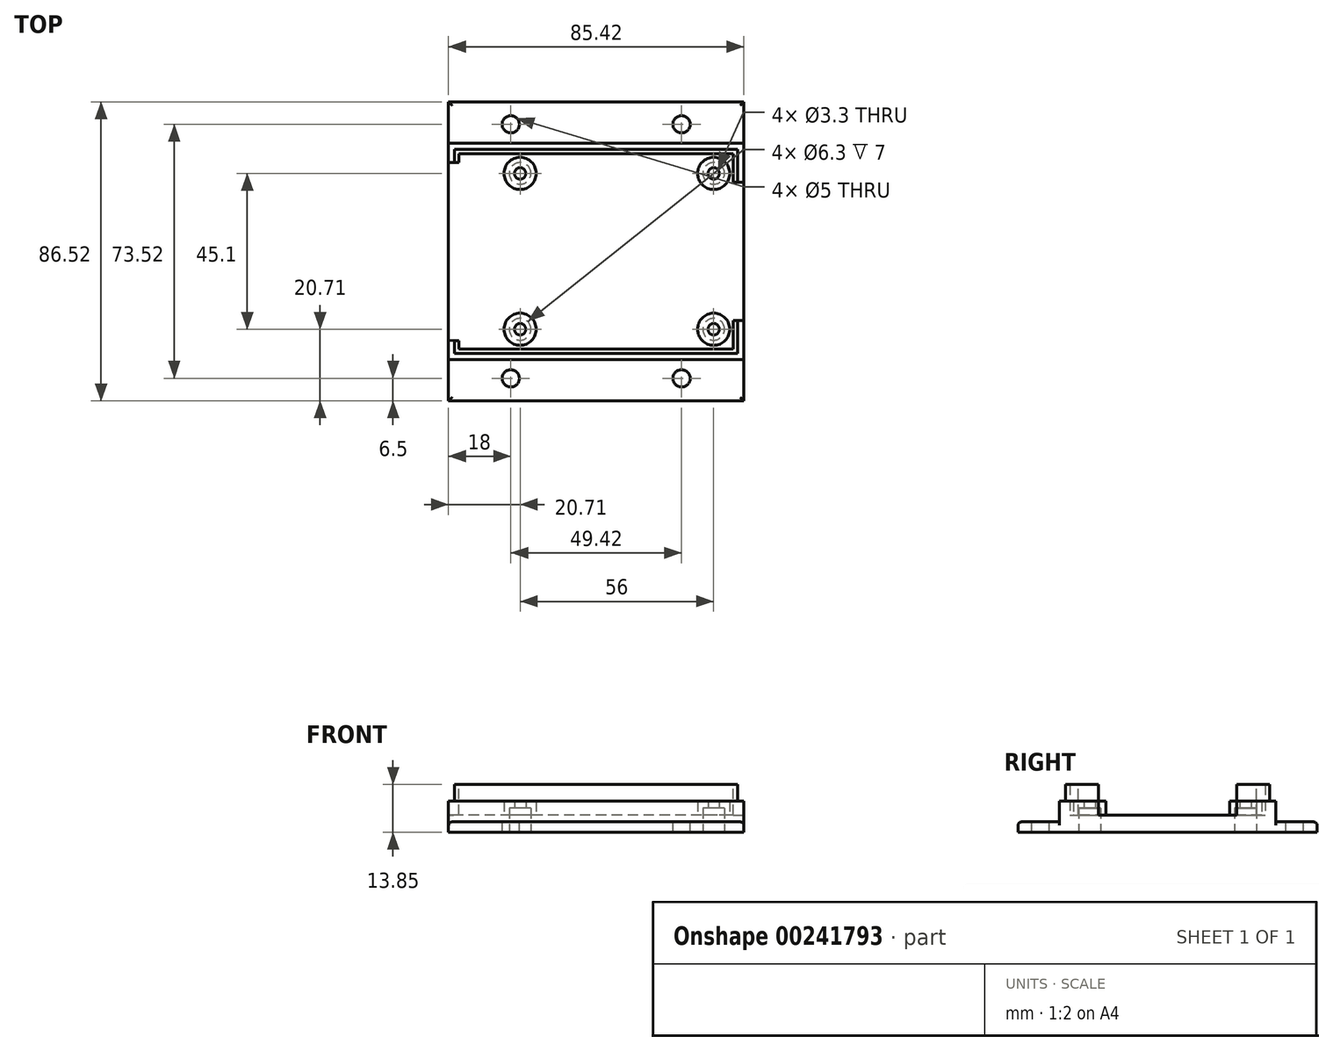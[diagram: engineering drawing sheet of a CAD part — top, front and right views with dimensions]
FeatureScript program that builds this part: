
annotation { "Feature Type Name" : "Feature", "Feature Type Description" : "" }
export const myFeature = defineFeature(function(context is Context, id is Id, definition is map)
    precondition{}
    {
        {
            var Q0;
            Q0=qCreatedBy(makeId("Top.planeOp"),FACE);
            var sketch = newSketch(context, id + "F0", { "sketchPlane" : qUnion([Q0])});
            skLineSegment(sketch, "E0.bottom", {"start": v(37.2, -25.76) * mm, "end": v(-37.2, -25.76) * mm, "construction": true});
            skLineSegment(sketch, "E0.top", {"start": v(37.2, 25.76) * mm, "end": v(-37.2, 25.76) * mm, "construction": true});
            skLineSegment(sketch, "E0.left", {"start": v(37.2, -25.76) * mm, "end": v(37.2, 25.76) * mm, "construction": true});
            skLineSegment(sketch, "E0.right", {"start": v(-37.2, -25.76) * mm, "end": v(-37.2, 25.76) * mm, "construction": true});
            skPoint(sketch, "E0.middle", {"position": v(0, 0) * mm});
            skCircle(sketch, "E1", {"center": v(-22, 22.55) * mm, "radius": 1.65 * mm});
            skCircle(sketch, "E2", {"center": v(34, 22.55) * mm, "radius": 1.65 * mm});
            skCircle(sketch, "E3", {"center": v(-22, -22.55) * mm, "radius": 1.65 * mm});
            skCircle(sketch, "E4", {"center": v(34, -22.55) * mm, "radius": 1.65 * mm});
            skLineSegment(sketch, "E5.0", {"start": v(39.7, 28.26) * mm, "end": v(-39.7, 28.26) * mm});
            skLineSegment(sketch, "E5.1", {"start": v(39.7, -28.26) * mm, "end": v(39.7, 28.26) * mm});
            skLineSegment(sketch, "E5.2", {"start": v(39.7, -28.26) * mm, "end": v(-39.7, -28.26) * mm});
            skLineSegment(sketch, "E5.3", {"start": v(-39.7, -28.26) * mm, "end": v(-39.7, 28.26) * mm});
            skLineSegment(sketch, "E6.0", {"start": v(41.2, 29.76) * mm, "end": v(-41.2, 29.76) * mm});
            skLineSegment(sketch, "E6.1", {"start": v(41.2, -29.76) * mm, "end": v(41.2, 29.76) * mm});
            skLineSegment(sketch, "E6.2", {"start": v(41.2, -29.76) * mm, "end": v(-41.2, -29.76) * mm});
            skLineSegment(sketch, "E6.3", {"start": v(-41.2, -29.76) * mm, "end": v(-41.2, 29.76) * mm});
            skLineSegment(sketch, "E7.0", {"start": v(42.7, 31.26) * mm, "end": v(-42.7, 31.26) * mm});
            skLineSegment(sketch, "E7.1", {"start": v(42.7, -31.26) * mm, "end": v(42.7, 31.26) * mm});
            skLineSegment(sketch, "E7.2", {"start": v(42.7, -31.26) * mm, "end": v(-42.7, -31.26) * mm});
            skLineSegment(sketch, "E7.3", {"start": v(-42.7, -31.26) * mm, "end": v(-42.7, 31.26) * mm});
            skCircle(sketch, "E8.0", {"center": v(-22, 22.55) * mm, "radius": 4.65 * mm});
            skCircle(sketch, "E9.0", {"center": v(34, 22.55) * mm, "radius": 4.65 * mm});
            skCircle(sketch, "E10.0", {"center": v(34, -22.55) * mm, "radius": 4.65 * mm});
            skCircle(sketch, "E11.0", {"center": v(-22, -22.55) * mm, "radius": 4.65 * mm});
            skCircle(sketch, "E12", {"center": v(-22, 22.55) * mm, "radius": 3.15 * mm});
            skCircle(sketch, "E13", {"center": v(34, 22.55) * mm, "radius": 3.15 * mm});
            skCircle(sketch, "E14", {"center": v(34, -22.55) * mm, "radius": 3.15 * mm});
            skCircle(sketch, "E15", {"center": v(-22, -22.55) * mm, "radius": 3.15 * mm});
            skSolve(sketch);
        }
        {
            var Q0;
            Q0=makeQuery(id+"F0.imprint","IMPRINT",FACE,{"disambiguationData":[TD([[makeQuery(id+"F0.imprint","IMPRINT",EDGE,{"derivedFrom":sQuery(id+"F0.wireOp",EDGE,"E5.0")}),1.0]])]});
            extrude(context, id + "F1", {"entities" : qUnion([Q0]), "depth" : 5 * mm, "offsetDistance" : 25 * mm});
        }
        {
            var Q0;
            Q0=makeQuery(id+"F0.imprint","IMPRINT",FACE,{"disambiguationData":[TD([[makeQuery(id+"F0.imprint","IMPRINT",EDGE,{"derivedFrom":sQuery(id+"F0.wireOp",EDGE,"E5.0")}),-1.0]])]});
            extrude(context, id + "F2", {"entities" : qUnion([Q0]), "operationType" : NewBodyOperationType.ADD, "depth" : 13.85 * mm, "offsetDistance" : 25 * mm});
        }
        {
            var Q0;
            Q0=makeQuery(id+"F0.imprint","IMPRINT",FACE,{"disambiguationData":[TD([[makeQuery(id+"F0.imprint","IMPRINT",EDGE,{"derivedFrom":sQuery(id+"F0.wireOp",EDGE,"E6.0")}),-1.0]])]});
            extrude(context, id + "F3", {"entities" : qUnion([Q0]), "operationType" : NewBodyOperationType.ADD, "depth" : 9 * mm, "offsetDistance" : 25 * mm});
        }
        {
            var Q0;
            Q0=makeQuery(id+"F2.opExtrude","CAP_FACE",FACE,{"disambiguationData":[OSD([sQuery(id+"F0.wireOp",EDGE,"E5.0"),sQuery(id+"F0.wireOp",EDGE,"E5.1"),sQuery(id+"F0.wireOp",EDGE,"E5.2"),sQuery(id+"F0.wireOp",EDGE,"E5.3"),sQuery(id+"F0.wireOp",EDGE,"E6.0"),sQuery(id+"F0.wireOp",EDGE,"E6.1"),sQuery(id+"F0.wireOp",EDGE,"E6.2"),sQuery(id+"F0.wireOp",EDGE,"E6.3")])],"isStart":false});
            var sketch = newSketch(context, id + "F4", { "sketchPlane" : qUnion([Q0])});
            skLineSegment(sketch, "E16", {"start": v(-39.7, 25.75) * mm, "end": v(-41.2, 25.75) * mm});
            skLineSegment(sketch, "E17", {"start": v(-39.7, -25.8) * mm, "end": v(-41.2, -25.8) * mm});
            skLineSegment(sketch, "E18", {"start": v(-41.2, 25.75) * mm, "end": v(-42.84, 25.75) * mm});
            skLineSegment(sketch, "E19", {"start": v(-42.84, 25.75) * mm, "end": v(-42.84, -25.8) * mm});
            skLineSegment(sketch, "E20", {"start": v(-42.84, -25.8) * mm, "end": v(-41.2, -25.8) * mm});
            skLineSegment(sketch, "E21", {"start": v(-39.7, -25.8) * mm, "end": v(-39.7, 25.75) * mm});
            skLineSegment(sketch, "E22", {"start": v(39.7, 19.96) * mm, "end": v(43.26, 19.96) * mm});
            skLineSegment(sketch, "E23", {"start": v(43.26, 19.96) * mm, "end": v(43.26, -19.96) * mm});
            skLineSegment(sketch, "E24", {"start": v(43.26, -19.96) * mm, "end": v(39.7, -19.96) * mm});
            skLineSegment(sketch, "E25", {"start": v(39.7, -19.96) * mm, "end": v(39.7, 19.96) * mm});
            skSolve(sketch);
        }
        {
            var Q0;
            {var subQ0=sQuery(id+"F4.wireOp",EDGE,"E18");Q0=makeQuery(id+"F4.imprint","IMPRINT",FACE,{"disambiguationData":[TD([[makeQuery(id+"F4.imprint","IMPRINT",EDGE,{"derivedFrom":subQ0}),1.0]])]});}
            var Q1;
            {var subQ0=sQuery(id+"F4.wireOp",EDGE,"E16");Q1=makeQuery(id+"F4.imprint","IMPRINT",FACE,{"disambiguationData":[TD([[makeQuery(id+"F4.imprint","IMPRINT",EDGE,{"derivedFrom":subQ0}),1.0]])]});}
            var Q2;
            {var subQ0=sQuery(id+"F4.wireOp",EDGE,"E25");Q2=makeQuery(id+"F4.imprint","IMPRINT",FACE,{"disambiguationData":[TD([[makeQuery(id+"F4.imprint","IMPRINT",EDGE,{"derivedFrom":subQ0}),-1.0]])]});}
            var Q3;
            {var subQ0=sQuery(id+"F4.wireOp",EDGE,"E23");Q3=makeQuery(id+"F4.imprint","IMPRINT",FACE,{"disambiguationData":[TD([[makeQuery(id+"F4.imprint","IMPRINT",EDGE,{"derivedFrom":subQ0}),-1.0]])]});}
            extrude(context, id + "F5", {"entities" : qUnion([Q0, Q1, Q2, Q3]), "operationType" : NewBodyOperationType.REMOVE, "oppositeDirection" : true, "depth" : 8.85 * mm, "offsetDistance" : 25 * mm});
        }
        {
            var Q0;
            Q0=makeQuery(id+"F0.imprint","IMPRINT",FACE,{"disambiguationData":[TD([[makeQuery(id+"F0.imprint","IMPRINT",EDGE,{"derivedFrom":sQuery(id+"F0.wireOp",EDGE,"E8.0")}),1.0]])]});
            var Q1;
            Q1=makeQuery(id+"F0.imprint","IMPRINT",FACE,{"disambiguationData":[TD([[makeQuery(id+"F0.imprint","IMPRINT",EDGE,{"derivedFrom":sQuery(id+"F0.wireOp",EDGE,"E9.0")}),1.0]])]});
            var Q2;
            Q2=makeQuery(id+"F0.imprint","IMPRINT",FACE,{"disambiguationData":[TD([[makeQuery(id+"F0.imprint","IMPRINT",EDGE,{"derivedFrom":sQuery(id+"F0.wireOp",EDGE,"E11.0")}),1.0]])]});
            var Q3;
            Q3=makeQuery(id+"F0.imprint","IMPRINT",FACE,{"disambiguationData":[TD([[makeQuery(id+"F0.imprint","IMPRINT",EDGE,{"derivedFrom":sQuery(id+"F0.wireOp",EDGE,"E10.0")}),1.0]])]});
            var Q4;
            Q4=makeQuery(id+"F0.imprint","IMPRINT",FACE,{"disambiguationData":[TD([[makeQuery(id+"F0.imprint","IMPRINT",EDGE,{"derivedFrom":sQuery(id+"F0.wireOp",EDGE,"E3")}),-1.0]])]});
            var Q5;
            Q5=makeQuery(id+"F0.imprint","IMPRINT",FACE,{"disambiguationData":[TD([[makeQuery(id+"F0.imprint","IMPRINT",EDGE,{"derivedFrom":sQuery(id+"F0.wireOp",EDGE,"E1")}),-1.0]])]});
            var Q6;
            Q6=makeQuery(id+"F0.imprint","IMPRINT",FACE,{"disambiguationData":[TD([[makeQuery(id+"F0.imprint","IMPRINT",EDGE,{"derivedFrom":sQuery(id+"F0.wireOp",EDGE,"E2")}),-1.0]])]});
            var Q7;
            Q7=makeQuery(id+"F0.imprint","IMPRINT",FACE,{"disambiguationData":[TD([[makeQuery(id+"F0.imprint","IMPRINT",EDGE,{"derivedFrom":sQuery(id+"F0.wireOp",EDGE,"E4")}),-1.0]])]});
            extrude(context, id + "F6", {"entities" : qUnion([Q0, Q1, Q2, Q3, Q4, Q5, Q6, Q7]), "operationType" : NewBodyOperationType.ADD, "depth" : 9 * mm, "offsetDistance" : 25 * mm});
        }
        {
            var Q0;
            Q0=makeQuery(id+"F0.imprint","IMPRINT",FACE,{"disambiguationData":[TD([[makeQuery(id+"F0.imprint","IMPRINT",EDGE,{"derivedFrom":sQuery(id+"F0.wireOp",EDGE,"E3")}),-1.0]])]});
            var Q1;
            Q1=makeQuery(id+"F0.imprint","IMPRINT",FACE,{"disambiguationData":[TD([[makeQuery(id+"F0.imprint","IMPRINT",EDGE,{"derivedFrom":sQuery(id+"F0.wireOp",EDGE,"E4")}),-1.0]])]});
            var Q2;
            Q2=makeQuery(id+"F0.imprint","IMPRINT",FACE,{"disambiguationData":[TD([[makeQuery(id+"F0.imprint","IMPRINT",EDGE,{"derivedFrom":sQuery(id+"F0.wireOp",EDGE,"E2")}),-1.0]])]});
            var Q3;
            Q3=makeQuery(id+"F0.imprint","IMPRINT",FACE,{"disambiguationData":[TD([[makeQuery(id+"F0.imprint","IMPRINT",EDGE,{"derivedFrom":sQuery(id+"F0.wireOp",EDGE,"E1")}),-1.0]])]});
            extrude(context, id + "F7", {"entities" : qUnion([Q0, Q1, Q2, Q3]), "operationType" : NewBodyOperationType.REMOVE, "depth" : 7 * mm, "offsetDistance" : 25 * mm});
        }
        {
            var Q0;
            Q0=makeQuery(id+"F3.opExtrude","SWEPT_FACE",FACE,{"disambiguationData":[OSD([sQuery(id+"F0.wireOp",EDGE,"E7.2")])]});
            var sketch = newSketch(context, id + "F8", { "sketchPlane" : qUnion([Q0])});
            skLineSegment(sketch, "E26.bottom", {"start": v(-42.71, 0) * mm, "end": v(42.7, 0) * mm});
            skLineSegment(sketch, "E26.top", {"start": v(-42.71, 3) * mm, "end": v(42.7, 3) * mm});
            skLineSegment(sketch, "E26.left", {"start": v(-42.71, 0) * mm, "end": v(-42.71, 3) * mm});
            skLineSegment(sketch, "E26.right", {"start": v(42.7, 0) * mm, "end": v(42.7, 3) * mm});
            skSolve(sketch);
        }
        {
            var Q0;
            Q0=makeQuery(id+"F3.opExtrude","SWEPT_FACE",FACE,{"disambiguationData":[OSD([sQuery(id+"F0.wireOp",EDGE,"E7.0")])]});
            var sketch = newSketch(context, id + "F9", { "sketchPlane" : qUnion([Q0])});
            skLineSegment(sketch, "E27.bottom", {"start": v(42.7, 0) * mm, "end": v(-42.71, 0) * mm});
            skLineSegment(sketch, "E27.top", {"start": v(42.7, 3) * mm, "end": v(-42.71, 3) * mm});
            skLineSegment(sketch, "E27.left", {"start": v(42.7, 0) * mm, "end": v(42.7, 3) * mm});
            skLineSegment(sketch, "E27.right", {"start": v(-42.71, 0) * mm, "end": v(-42.71, 3) * mm});
            skSolve(sketch);
        }
        {
            var Q0;
            Q0=makeQuery(id+"F9.imprint","IMPRINT",FACE,{"disambiguationData":[TD([[makeQuery(id+"F9.imprint","IMPRINT",EDGE,{"derivedFrom":sQuery(id+"F9.wireOp",EDGE,"E27.bottom")}),1.0]])]});
            extrude(context, id + "F10", {"entities" : qUnion([Q0]), "operationType" : NewBodyOperationType.ADD, "depth" : 12 * mm});
        }
        {
            var Q0;
            Q0=makeQuery(id+"F8.imprint","IMPRINT",FACE,{"disambiguationData":[TD([[makeQuery(id+"F8.imprint","IMPRINT",EDGE,{"derivedFrom":sQuery(id+"F8.wireOp",EDGE,"E26.bottom")}),-1.0]])]});
            extrude(context, id + "F11", {"entities" : qUnion([Q0]), "operationType" : NewBodyOperationType.ADD, "depth" : 12 * mm});
        }
        {
            var Q0;
            Q0=makeQuery(id+"F11.opExtrude","SWEPT_EDGE",EDGE,{"disambiguationData":[OSD([sQuery(id+"F0.wireOp",EDGE,"E7.1"),sQuery(id+"F0.wireOp",EDGE,"E7.2"),sQuery(id+"F8.wireOp",EDGE,"E26.top"),sQuery(id+"F8.wireOp",EDGE,"E26.right")])]});
            var Q1;
            Q1=makeQuery(id+"F11.opExtrude","CAP_EDGE",EDGE,{"disambiguationData":[OSD([sQuery(id+"F8.wireOp",EDGE,"E26.top")])],"isStart":false});
            var Q2;
            Q2=makeQuery(id+"F11.opExtrude","SWEPT_EDGE",EDGE,{"disambiguationData":[OSD([sQuery(id+"F0.wireOp",EDGE,"E7.2"),sQuery(id+"F0.wireOp",EDGE,"E7.3"),sQuery(id+"F8.wireOp",EDGE,"E26.top"),sQuery(id+"F8.wireOp",EDGE,"E26.left")])]});
            var Q3;
            Q3=makeQuery(id+"F10.opExtrude","SWEPT_EDGE",EDGE,{"disambiguationData":[OSD([sQuery(id+"F0.wireOp",EDGE,"E7.0"),sQuery(id+"F0.wireOp",EDGE,"E7.3"),sQuery(id+"F9.wireOp",EDGE,"E27.top"),sQuery(id+"F9.wireOp",EDGE,"E27.left")])]});
            var Q4;
            Q4=makeQuery(id+"F10.opExtrude","CAP_EDGE",EDGE,{"disambiguationData":[OSD([sQuery(id+"F9.wireOp",EDGE,"E27.top")])],"isStart":false});
            var Q5;
            Q5=makeQuery(id+"F10.opExtrude","SWEPT_EDGE",EDGE,{"disambiguationData":[OSD([sQuery(id+"F0.wireOp",EDGE,"E7.0"),sQuery(id+"F0.wireOp",EDGE,"E7.1"),sQuery(id+"F9.wireOp",EDGE,"E27.top"),sQuery(id+"F9.wireOp",EDGE,"E27.right")])]});
            fillet(context, id + "F12", {"entities" : qUnion([Q0, Q1, Q2, Q3, Q4, Q5]), "radius" : 1 * mm, "tangentPropagation" : true, "allowEdgeOverflow" : false});
        }
        {
            var Q0;
            Q0=makeQuery(id+"F10.opExtrude","SWEPT_FACE",FACE,{"disambiguationData":[OSD([sQuery(id+"F9.wireOp",EDGE,"E27.top")])]});
            var sketch = newSketch(context, id + "F13", { "sketchPlane" : qUnion([Q0])});
            skLineSegment(sketch, "E28", {"start": v(-41.7, 36.76) * mm, "end": v(41.7, 36.76) * mm, "construction": true});
            skCircle(sketch, "E29", {"center": v(-24.7, 36.76) * mm, "radius": 2.5 * mm});
            skCircle(sketch, "E30", {"center": v(24.7, 36.76) * mm, "radius": 2.5 * mm});
            skSolve(sketch);
        }
        {
            var Q0;
            Q0=makeQuery(id+"F11.opExtrude","SWEPT_FACE",FACE,{"disambiguationData":[OSD([sQuery(id+"F8.wireOp",EDGE,"E26.top")])]});
            var sketch = newSketch(context, id + "F14", { "sketchPlane" : qUnion([Q0])});
            skLineSegment(sketch, "E31", {"start": v(-41.7, -36.76) * mm, "end": v(41.7, -36.76) * mm, "construction": true});
            skCircle(sketch, "E32", {"center": v(-24.7, -36.76) * mm, "radius": 2.5 * mm});
            skCircle(sketch, "E33", {"center": v(24.7, -36.76) * mm, "radius": 2.5 * mm});
            skSolve(sketch);
        }
        {
            var Q0;
            Q0=makeQuery(id+"F13.imprint","IMPRINT",FACE,{"disambiguationData":[TD([[makeQuery(id+"F13.imprint","IMPRINT",EDGE,{"derivedFrom":sQuery(id+"F13.wireOp",EDGE,"E29")}),1.0]])]});
            var Q1;
            Q1=makeQuery(id+"F13.imprint","IMPRINT",FACE,{"disambiguationData":[TD([[makeQuery(id+"F13.imprint","IMPRINT",EDGE,{"derivedFrom":sQuery(id+"F13.wireOp",EDGE,"E30")}),1.0]])]});
            var Q2;
            Q2=makeQuery(id+"F14.imprint","IMPRINT",FACE,{"disambiguationData":[TD([[makeQuery(id+"F14.imprint","IMPRINT",EDGE,{"derivedFrom":sQuery(id+"F14.wireOp",EDGE,"E32")}),1.0]])]});
            var Q3;
            Q3=makeQuery(id+"F14.imprint","IMPRINT",FACE,{"disambiguationData":[TD([[makeQuery(id+"F14.imprint","IMPRINT",EDGE,{"derivedFrom":sQuery(id+"F14.wireOp",EDGE,"E33")}),1.0]])]});
            extrude(context, id + "F15", {"entities" : qUnion([Q0, Q1, Q2, Q3]), "operationType" : NewBodyOperationType.REMOVE, "oppositeDirection" : true, "depth" : 3 * mm});
        }
        {
            var Q0;
            {var subQ0=sQuery(id+"F0.wireOp",EDGE,"E6.1");var subQ1=sQuery(id+"F0.wireOp",EDGE,"E5.3");var subQ2=sQuery(id+"F0.wireOp",EDGE,"E5.2");var subQ3=sQuery(id+"F0.wireOp",EDGE,"E5.1");var subQ4=sQuery(id+"F0.wireOp",EDGE,"E6.2");var subQ5=sQuery(id+"F0.wireOp",EDGE,"E6.3");Q0=makeQuery(id+"F5.boolean.opBoolean","SPLIT",FACE,{"disambiguationData":[TD([makeQuery(id+"F2.opExtrude","SWEPT_FACE",FACE,{"disambiguationData":[OSD([subQ2])]})])],"derivedFrom":makeQuery(id+"F2.opExtrude","CAP_FACE",FACE,{"disambiguationData":[OSD([sQuery(id+"F0.wireOp",EDGE,"E5.0"),subQ3,subQ2,subQ1,sQuery(id+"F0.wireOp",EDGE,"E6.0"),subQ0,subQ4,subQ5])],"isStart":false})});}
            var sketch = newSketch(context, id + "F16", { "sketchPlane" : qUnion([Q0])});
            skLineSegment(sketch, "E34.0", {"start": v(40.96, -29.51) * mm, "end": v(40.96, -15.76) * mm});
            skLineSegment(sketch, "E34.1", {"start": v(40.96, -29.51) * mm, "end": v(-40.96, -29.51) * mm});
            skLineSegment(sketch, "E34.2", {"start": v(-40.96, -29.51) * mm, "end": v(-40.96, -25.8) * mm});
            skSolve(sketch);
        }
        {
            var Q0;
            {var subQ0=sQuery(id+"F0.wireOp",EDGE,"E6.0");var subQ1=sQuery(id+"F0.wireOp",EDGE,"E5.1");var subQ2=sQuery(id+"F0.wireOp",EDGE,"E5.3");var subQ3=sQuery(id+"F0.wireOp",EDGE,"E5.0");var subQ4=sQuery(id+"F0.wireOp",EDGE,"E6.1");var subQ5=sQuery(id+"F0.wireOp",EDGE,"E6.3");Q0=makeQuery(id+"F5.boolean.opBoolean","SPLIT",FACE,{"disambiguationData":[TD([makeQuery(id+"F2.opExtrude","SWEPT_FACE",FACE,{"disambiguationData":[OSD([subQ3])]})])],"derivedFrom":makeQuery(id+"F2.opExtrude","CAP_FACE",FACE,{"disambiguationData":[OSD([subQ3,subQ1,sQuery(id+"F0.wireOp",EDGE,"E5.2"),subQ2,subQ0,subQ4,sQuery(id+"F0.wireOp",EDGE,"E6.2"),subQ5])],"isStart":false})});}
            var sketch = newSketch(context, id + "F17", { "sketchPlane" : qUnion([Q0])});
            skLineSegment(sketch, "E35.0", {"start": v(-40.96, 25.75) * mm, "end": v(-40.96, 29.5) * mm});
            skLineSegment(sketch, "E35.1", {"start": v(40.96, 29.5) * mm, "end": v(-40.96, 29.5) * mm});
            skLineSegment(sketch, "E35.2", {"start": v(40.96, 15.76) * mm, "end": v(40.96, 29.5) * mm});
            skSolve(sketch);
        }
        {
            var Q0;
            {var subQ9=sQuery(id+"F17.wireOp",EDGE,"E35.0");Q0=makeQuery(id+"F17.imprint","IMPRINT",FACE,{"disambiguationData":[TD([[makeQuery(id+"F17.imprint","IMPRINT",EDGE,{"derivedFrom":subQ9}),1.0]])]});}
            var Q1;
            {var subQ9=sQuery(id+"F16.wireOp",EDGE,"E34.0");Q1=makeQuery(id+"F16.imprint","IMPRINT",FACE,{"disambiguationData":[TD([[makeQuery(id+"F16.imprint","IMPRINT",EDGE,{"derivedFrom":subQ9}),-1.0]])]});}
            extrude(context, id + "F18", {"entities" : qUnion([Q0, Q1]), "operationType" : NewBodyOperationType.REMOVE, "oppositeDirection" : true, "depth" : 4.85 * mm, "offsetDistance" : 25 * mm});
        }
    });
